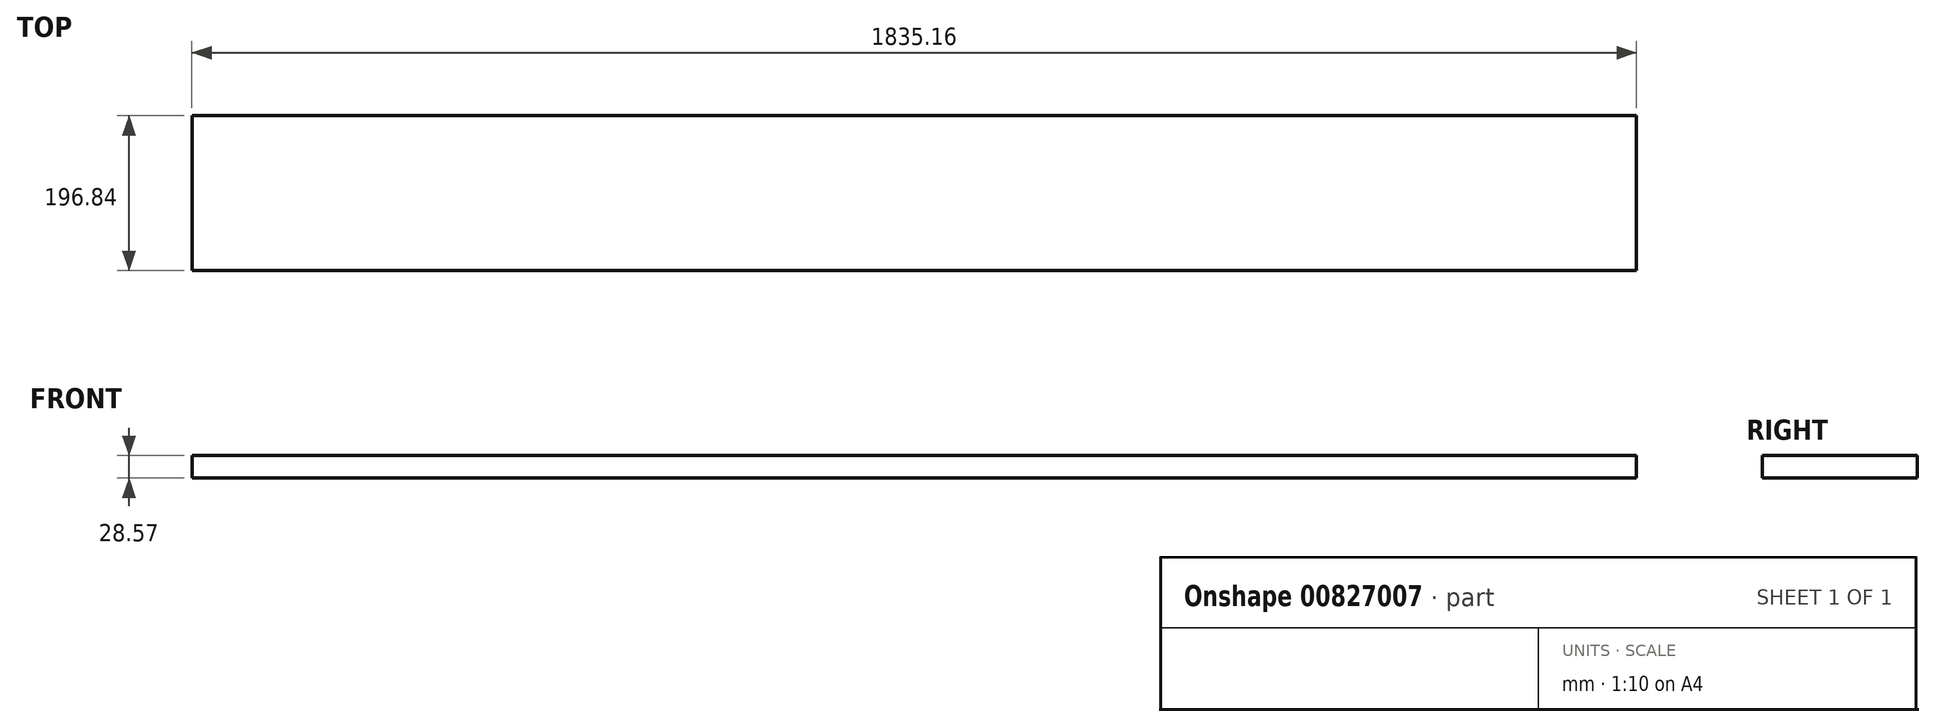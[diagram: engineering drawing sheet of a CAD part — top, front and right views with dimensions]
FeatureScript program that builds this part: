
annotation { "Feature Type Name" : "Feature", "Feature Type Description" : "" }
export const myFeature = defineFeature(function(context is Context, id is Id, definition is map)
    precondition{}
    {
        {
            var Q0;
            Q0=qCreatedBy(makeId("Top.planeOp"),FACE);
            var sketch = newSketch(context, id + "F0", { "sketchPlane" : qUnion([Q0])});
            skLineSegment(sketch, "E0.bottom", {"start": v(-917.58, 98.43) * mm, "end": v(917.58, 98.43) * mm});
            skLineSegment(sketch, "E0.top", {"start": v(-917.58, -98.42) * mm, "end": v(917.58, -98.42) * mm});
            skLineSegment(sketch, "E0.left", {"start": v(-917.58, 98.43) * mm, "end": v(-917.58, -98.42) * mm});
            skLineSegment(sketch, "E0.right", {"start": v(917.58, 98.43) * mm, "end": v(917.58, -98.42) * mm});
            skPoint(sketch, "E0.middle", {"position": v(0, 0) * mm});
            skSolve(sketch);
        }
        {
            var Q0;
            Q0=makeQuery(id+"F0.imprint","IMPRINT",FACE,{"disambiguationData":[TD([[makeQuery(id+"F0.imprint","IMPRINT",EDGE,{"derivedFrom":sQuery(id+"F0.wireOp",EDGE,"E0.bottom")}),-1.0]])]});
            extrude(context, id + "F1", {"entities" : qUnion([Q0]), "depth" : 28.57 * mm, "offsetDistance" : 25.4 * mm});
        }
    });
